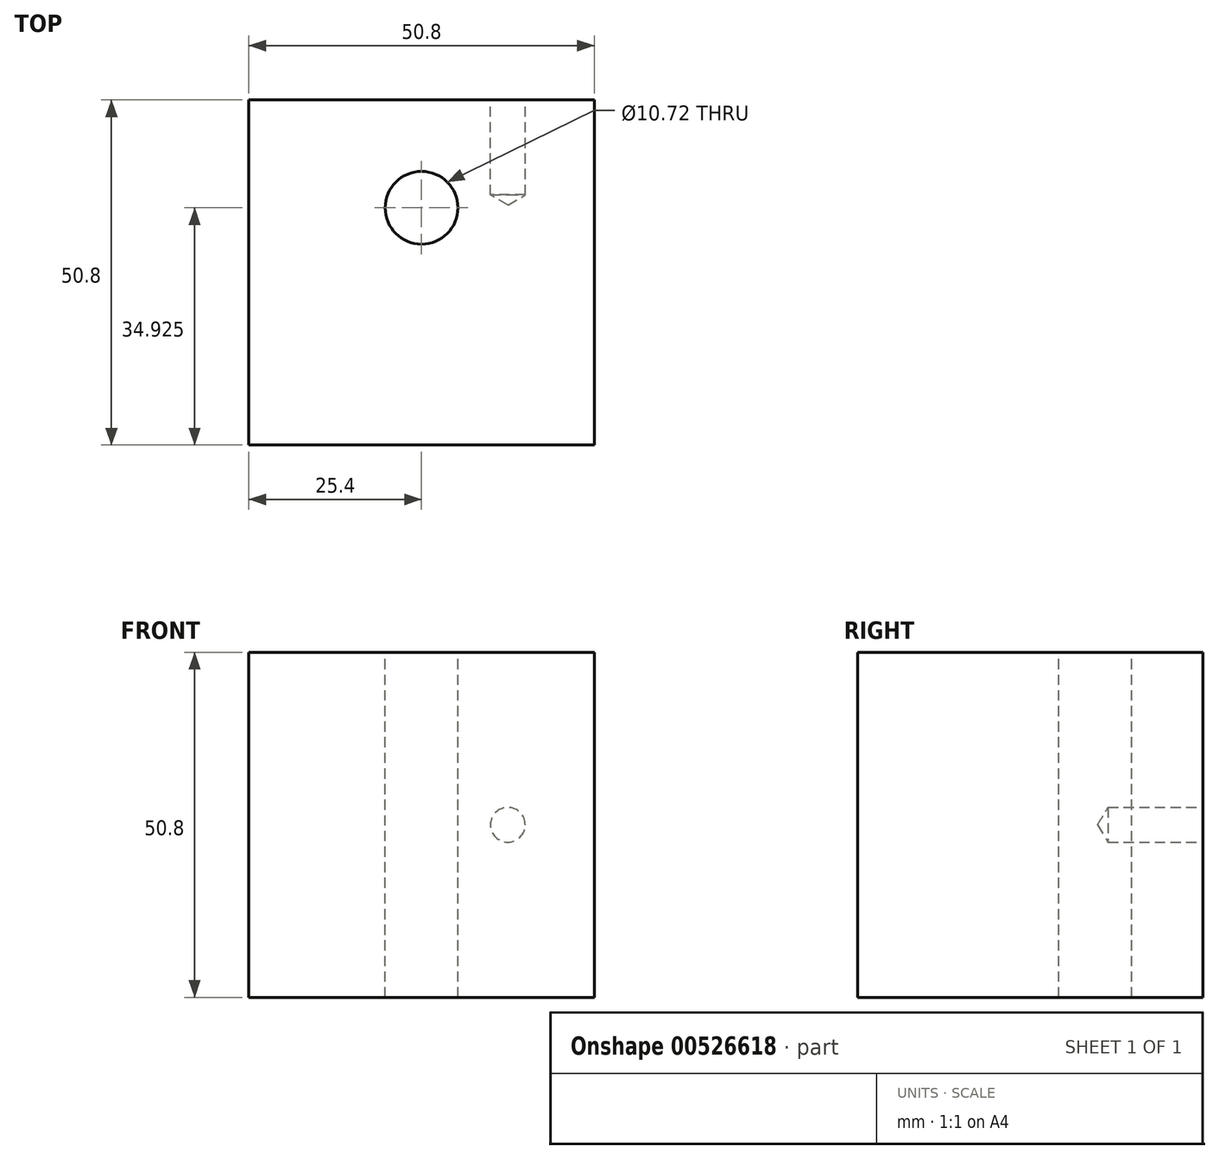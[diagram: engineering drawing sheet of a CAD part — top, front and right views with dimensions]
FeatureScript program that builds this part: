
annotation { "Feature Type Name" : "Feature", "Feature Type Description" : "" }
export const myFeature = defineFeature(function(context is Context, id is Id, definition is map)
    precondition{}
    {
        {
            var Q0;
            Q0=qCreatedBy(makeId("Top.planeOp"),FACE);
            var sketch = newSketch(context, id + "F0", { "sketchPlane" : qUnion([Q0])});
            skLineSegment(sketch, "E0.bottom", {"start": v(0, 0) * mm, "end": v(-50.8, 0) * mm});
            skLineSegment(sketch, "E0.top", {"start": v(0, 50.8) * mm, "end": v(-50.8, 50.8) * mm});
            skLineSegment(sketch, "E0.left", {"start": v(0, 0) * mm, "end": v(0, 50.8) * mm});
            skLineSegment(sketch, "E0.right", {"start": v(-50.8, 0) * mm, "end": v(-50.8, 50.8) * mm});
            skSolve(sketch);
        }
        {
            var Q0;
            Q0 = qSketchRegion(id + "F0", true);
            extrude(context, id + "F1", {"entities" : qUnion([Q0]), "depth" : 50.8 * mm, "offsetDistance" : 25.4 * mm});
        }
        {
            var Q0;
            Q0=makeQuery(id+"F1.opExtrude","CAP_FACE",FACE,{"disambiguationData":[OSD([sQuery(id+"F0.wireOp",EDGE,"E0.bottom"),sQuery(id+"F0.wireOp",EDGE,"E0.top"),sQuery(id+"F0.wireOp",EDGE,"E0.left"),sQuery(id+"F0.wireOp",EDGE,"E0.right")])],"isStart":false});
            var sketch = newSketch(context, id + "F2", { "sketchPlane" : qUnion([Q0])});
            skPoint(sketch, "E1", {"position": v(-25.4, 34.93) * mm});
            skSolve(sketch);
        }
        {
            var Q0;
            Q0=sQuery(id+"F2.wireOp",VERTEX,"E1");
            var Q1;
            Q1=makeQuery(id+"F1.opExtrude","SWEPT_BODY",BODY,{"disambiguationData":[OSD([sQuery(id+"F0.wireOp",EDGE,"E0.bottom"),sQuery(id+"F0.wireOp",EDGE,"E0.top"),sQuery(id+"F0.wireOp",EDGE,"E0.left"),sQuery(id+"F0.wireOp",EDGE,"E0.right")])]});
            hole(context, id + "F3", {"style" : HoleStyle.SIMPLE, "endStyle" : HoleEndStyle.THROUGH, "standardTappedOrClearance" : lookupTablePath({ "standard" : "ANSI", "engagement" : "75%", "pitch" : "13 tpi", "size" : "1/2", "type" : "Tapped" }), "standardBlindInLast" : lookupTablePath({ "standard" : "ANSI", "engagement" : "75%", "pitch" : "13 tpi", "size" : "1/2", "type" : "Tapped" }), "holeDiameter" : 10.72 * mm, "showTappedDepth" : true, "isTappedThrough" : true, "tappedDepth" : 8.9 * mm, "tapClearance" : 1, "locations" : qUnion([Q0]), "scope" : qUnion([Q1]), "majorDiameter" : 12.7 * mm});
        }
        {
            var Q0;
            Q0=makeQuery(id+"F1.opExtrude","SWEPT_FACE",FACE,{"disambiguationData":[OSD([sQuery(id+"F0.wireOp",EDGE,"E0.top")])]});
            var sketch = newSketch(context, id + "F4", { "sketchPlane" : qUnion([Q0])});
            skPoint(sketch, "E2", {"position": v(12.7, 25.4) * mm});
            skSolve(sketch);
        }
        {
            var Q0;
            Q0=sQuery(id+"F4.wireOp",VERTEX,"E2");
            var Q1;
            Q1=makeQuery(id+"F1.opExtrude","SWEPT_BODY",BODY,{"disambiguationData":[OSD([sQuery(id+"F0.wireOp",EDGE,"E0.bottom"),sQuery(id+"F0.wireOp",EDGE,"E0.top"),sQuery(id+"F0.wireOp",EDGE,"E0.left"),sQuery(id+"F0.wireOp",EDGE,"E0.right")])]});
            hole(context, id + "F5", {"style" : HoleStyle.SIMPLE, "endStyle" : HoleEndStyle.BLIND, "standardTappedOrClearance" : lookupTablePath({ "standard" : "ANSI", "engagement" : "75%", "pitch" : "20 tpi", "size" : "1/4", "type" : "Tapped" }), "standardBlindInLast" : lookupTablePath({ "standard" : "ANSI", "engagement" : "75%", "pitch" : "20 tpi", "size" : "1/4", "type" : "Tapped" }), "holeDiameter" : 5.1 * mm, "showTappedDepth" : true, "holeDepth" : 13.97 * mm, "isTappedThrough" : true, "tappedDepth" : 12.7 * mm, "tapClearance" : 1, "locations" : qUnion([Q0]), "scope" : qUnion([Q1]), "majorDiameter" : 6.35 * mm});
        }
    });
